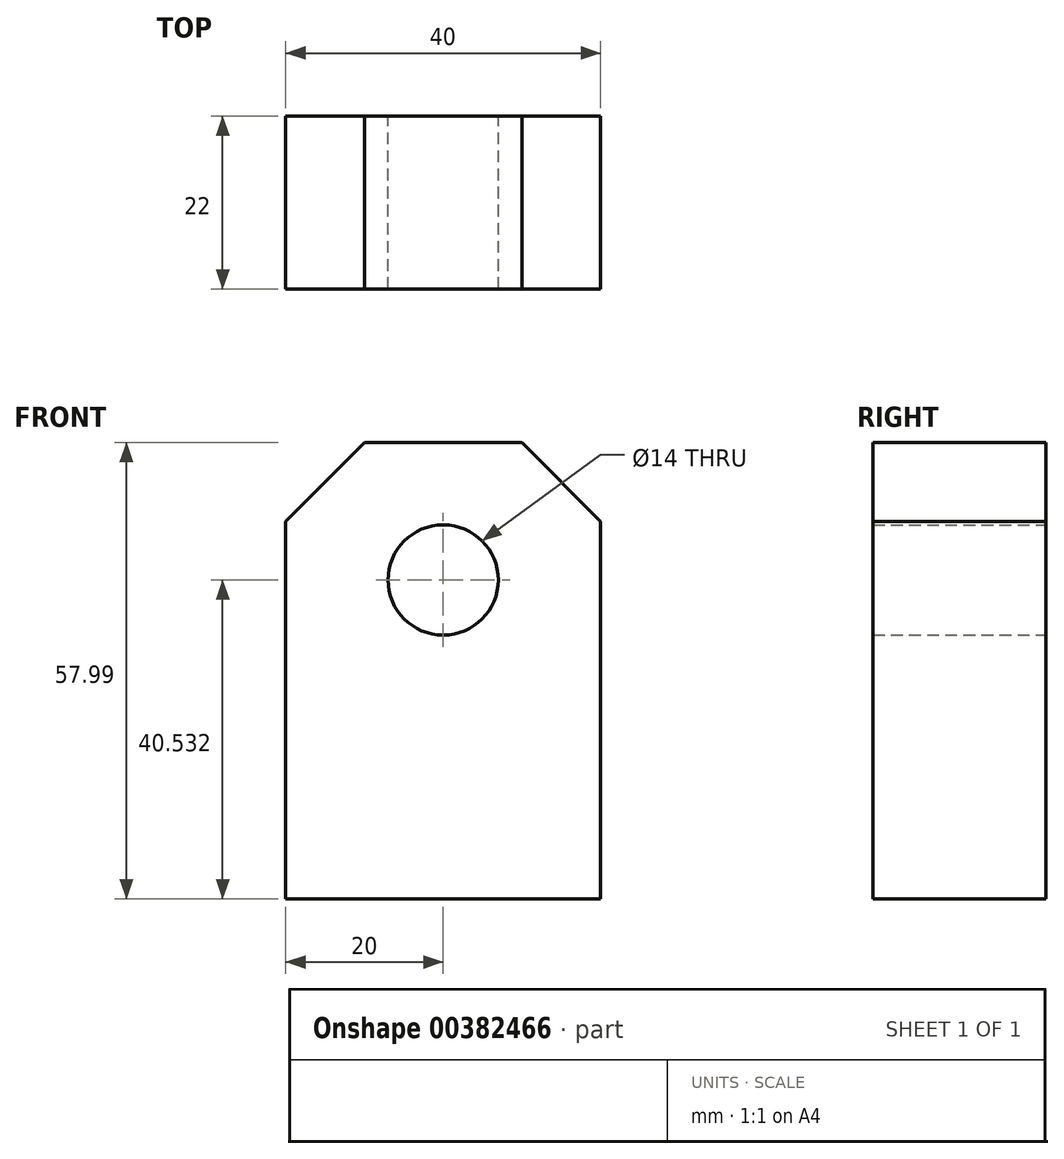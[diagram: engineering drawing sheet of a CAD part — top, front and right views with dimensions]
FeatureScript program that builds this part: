
annotation { "Feature Type Name" : "Feature", "Feature Type Description" : "" }
export const myFeature = defineFeature(function(context is Context, id is Id, definition is map)
    precondition{}
    {
        {
            var Q0;
            Q0=qCreatedBy(makeId("Front.planeOp"),FACE);
            var sketch = newSketch(context, id + "F0", { "sketchPlane" : qUnion([Q0])});
            skLineSegment(sketch, "E0.bottom", {"start": v(20, -31.36) * mm, "end": v(-20, -31.36) * mm});
            skLineSegment(sketch, "E0.top", {"start": v(20, 26.63) * mm, "end": v(-20, 26.63) * mm});
            skLineSegment(sketch, "E0.left", {"start": v(20, -31.36) * mm, "end": v(20, 26.63) * mm});
            skLineSegment(sketch, "E0.right", {"start": v(-20, -31.36) * mm, "end": v(-20, 26.63) * mm});
            skCircle(sketch, "E1", {"center": v(0, 9.17) * mm, "radius": 7 * mm});
            skSolve(sketch);
        }
        {
            var Q0;
            Q0 = qSketchRegion(id + "F0", true);
            extrude(context, id + "F1", {"entities" : qUnion([Q0]), "depth" : 22 * mm});
        }
        {
            var Q0;
            Q0=makeQuery(id+"F1.opExtrude","SWEPT_EDGE",EDGE,{"disambiguationData":[OSD([sQuery(id+"F0.wireOp",EDGE,"E0.top"),sQuery(id+"F0.wireOp",EDGE,"E0.left")])]});
            var Q1;
            Q1=makeQuery(id+"F1.opExtrude","SWEPT_EDGE",EDGE,{"disambiguationData":[OSD([sQuery(id+"F0.wireOp",EDGE,"E0.top"),sQuery(id+"F0.wireOp",EDGE,"E0.right")])]});
            chamfer(context, id + "F2", {"entities" : qUnion([Q0, Q1]), "width" : 10 * mm, "tangentPropagation" : true});
        }
    });
